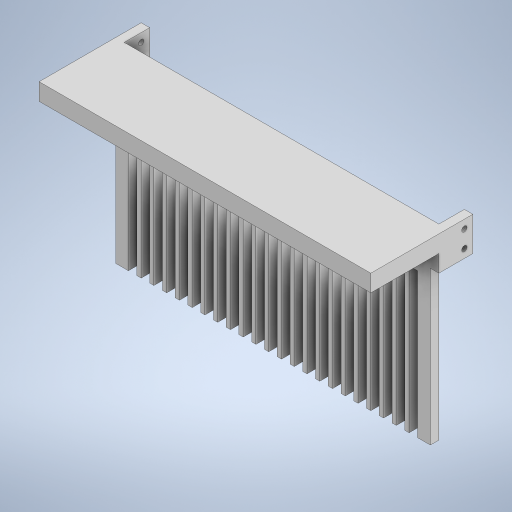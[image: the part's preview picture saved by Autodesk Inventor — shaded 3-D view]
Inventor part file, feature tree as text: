
AUTODESK INVENTOR PART (.ipt)
format: ipt  version: 2023.1 (Build 271208000, 208)  size: 346,112 bytes
history: native  units: mm
features: sketch x5, extrude x4, pattern_linear x1, hole x1, mirror x1
ambient origin geometry x8: Origin, YZ Plane, XZ Plane, XY Plane, X Axis, Y Axis, Z Axis, Center Point
bodies: 实体1 (feature_tree)
feature tree (12):
  extrude  "拉伸1"  Depth=220.0mm
  extrude  "拉伸2"  Depth=15.0mm
  pattern_linear  "矩形阵列1"  Count1=5  [1 undecoded]
  extrude  "拉伸3"  Depth=230.0mm
  hole  "孔2"  [1 undecoded]
  mirror  "镜像2"
  extrude  "拉伸4"  Depth=10.0mm TaperAngle=0.0deg
  sketch  "草图1"  dims[d0=370.0mm d1=220.0mm]
  sketch  "草图2"  dims[d3=10.0mm d4=0.0mm d5=15.0mm]
  sketch  "草图3"  dims[d6=10.0mm d7=50.0mm]
  sketch  "草图5"  dims[d8=0.0mm d9=0.0mm d10=230.0mm d12=15.0mm]
  sketch  "草图6"  dims[d13=40.0mm d14=40.0mm d15=10.0mm d16=0.0mm d28=6.4008mm d29=6.0mm d30=4.0mm d31=2.0mm d32=90.0deg d33=8.0mm d34=20.594885mm d35=20.0mm d36=20.0mm d37=10.0mm d38=80.0mm d39=0.0mm d17=1.0mm d18=1.0mm d19=1.0mm d20=0.15mm d21=0.25mm d22=0.375mm d23=14.3117mm d24=0.75mm d25=20.594885mm d26=0.0625mm d27=0.75mm d40=0.5mm d41=0.872665mm d42=0.5mm d43=0.872665mm]
note: 2 required parameter values undecoded (feature->parameter linkage not recoverable at this tier; creation-order binding heuristic only, values carry confidence <= 0.55)
